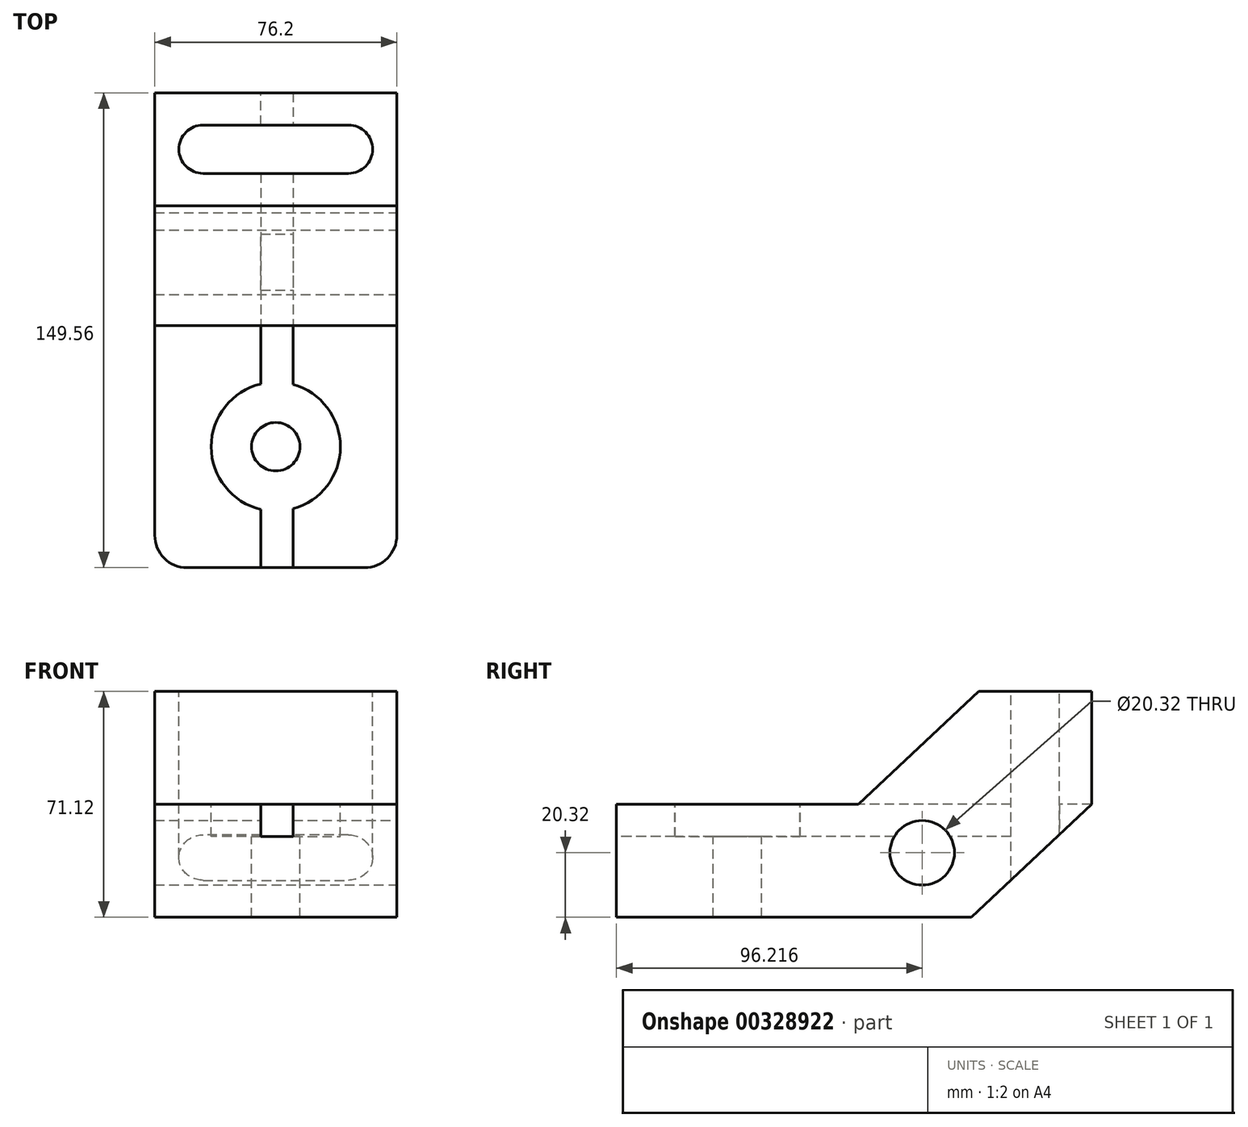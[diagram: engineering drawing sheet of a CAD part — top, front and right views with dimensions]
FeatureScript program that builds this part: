
annotation { "Feature Type Name" : "Feature", "Feature Type Description" : "" }
export const myFeature = defineFeature(function(context is Context, id is Id, definition is map)
    precondition{}
    {
        {
            var Q0;
            Q0=qCreatedBy(makeId("Right.planeOp"),FACE);
            var sketch = newSketch(context, id + "F0", { "sketchPlane" : qUnion([Q0])});
            skLineSegment(sketch, "E0.top", {"start": v(0, 35.56) * mm, "end": v(76.2, 35.56) * mm});
            skLineSegment(sketch, "E0.left", {"start": v(0, 0) * mm, "end": v(0, 35.56) * mm});
            skLineSegment(sketch, "E1", {"start": v(0, 0) * mm, "end": v(111.76, 0) * mm});
            skLineSegment(sketch, "E2", {"start": v(111.76, 0) * mm, "end": v(149.56, 35.56) * mm});
            skLineSegment(sketch, "E3", {"start": v(149.56, 35.56) * mm, "end": v(149.56, 71.12) * mm});
            skLineSegment(sketch, "E4", {"start": v(149.56, 71.12) * mm, "end": v(114, 71.12) * mm});
            skLineSegment(sketch, "E5", {"start": v(114, 71.12) * mm, "end": v(76.2, 35.56) * mm});
            skSolve(sketch);
        }
        {
            var Q0;
            Q0=makeQuery(id+"F0.imprint","IMPRINT",FACE,{"disambiguationData":[TD([[makeQuery(id+"F0.imprint","IMPRINT",EDGE,{"derivedFrom":sQuery(id+"F0.wireOp",EDGE,"E0.top")}),-1.0]])]});
            extrude(context, id + "F1", {"entities" : qUnion([Q0]), "oppositeDirection" : true, "depth" : 76.2 * mm});
        }
        {
            var Q0;
            Q0=makeQuery(id+"F1.opExtrude","CAP_EDGE",EDGE,{"disambiguationData":[OSD([sQuery(id+"F0.wireOp",EDGE,"E0.left")])],"isStart":false});
            var Q1;
            Q1=makeQuery(id+"F1.opExtrude","CAP_EDGE",EDGE,{"disambiguationData":[OSD([sQuery(id+"F0.wireOp",EDGE,"E0.left")])],"isStart":true});
            fillet(context, id + "F2", {"entities" : qUnion([Q0, Q1]), "radius" : 10.16 * mm, "tangentPropagation" : true, "allowEdgeOverflow" : false});
        }
        {
            var Q0;
            Q0=makeQuery(id+"F1.opExtrude","SWEPT_FACE",FACE,{"disambiguationData":[OSD([sQuery(id+"F0.wireOp",EDGE,"E0.top")])]});
            var sketch = newSketch(context, id + "F3", { "sketchPlane" : qUnion([Q0])});
            skCircle(sketch, "E6", {"center": v(-38.1, 38.1) * mm, "radius": 13.54 * mm});
            skLineSegment(sketch, "E7", {"start": v(-38.1, 38.1) * mm, "end": v(-33.02, 38.1) * mm});
            skLineSegment(sketch, "E8", {"start": v(-38.1, 38.1) * mm, "end": v(-43.18, 38.1) * mm});
            skLineSegment(sketch, "E9", {"start": v(-43.18, 38.1) * mm, "end": v(-43.18, 0) * mm});
            skLineSegment(sketch, "E10", {"start": v(-43.18, 0) * mm, "end": v(-33.02, 0) * mm});
            skLineSegment(sketch, "E11", {"start": v(-33.02, 0) * mm, "end": v(-33.02, 38.1) * mm});
            skLineSegment(sketch, "E12", {"start": v(-33.02, 38.1) * mm, "end": v(-33.02, 155.7) * mm});
            skLineSegment(sketch, "E13", {"start": v(-33.02, 155.7) * mm, "end": v(-43.18, 155.7) * mm});
            skLineSegment(sketch, "E14", {"start": v(-43.18, 155.7) * mm, "end": v(-43.18, 38.1) * mm});
            skSolve(sketch);
        }
        {
            var Q0;
            Q0=sQuery(id+"F3.wireOp",VERTEX,"E6.center");
            var Q1;
            Q1=makeQuery(id+"F1.opExtrude","SWEPT_BODY",BODY,{"disambiguationData":[OSD([sQuery(id+"F0.wireOp",EDGE,"E0.top"),sQuery(id+"F0.wireOp",EDGE,"E0.left"),sQuery(id+"F0.wireOp",EDGE,"E1"),sQuery(id+"F0.wireOp",EDGE,"E2"),sQuery(id+"F0.wireOp",EDGE,"E3"),sQuery(id+"F0.wireOp",EDGE,"E4"),sQuery(id+"F0.wireOp",EDGE,"E5")])]});
            hole(context, id + "F4", {"style" : HoleStyle.C_BORE, "endStyle" : HoleEndStyle.THROUGH, "holeDiameter" : 15.24 * mm, "cBoreDiameter" : 40.64 * mm, "cBoreDepth" : 10.16 * mm, "tappedDepth" : 12.7 * mm, "tapClearance" : 3, "locations" : qUnion([Q0]), "scope" : qUnion([Q1])});
        }
        {
            var Q0;
            Q0=makeQuery(id+"F1.opExtrude","CAP_FACE",FACE,{"disambiguationData":[OSD([sQuery(id+"F0.wireOp",EDGE,"E0.top"),sQuery(id+"F0.wireOp",EDGE,"E0.left"),sQuery(id+"F0.wireOp",EDGE,"E1"),sQuery(id+"F0.wireOp",EDGE,"E2"),sQuery(id+"F0.wireOp",EDGE,"E3"),sQuery(id+"F0.wireOp",EDGE,"E4"),sQuery(id+"F0.wireOp",EDGE,"E5")])],"isStart":true});
            var sketch = newSketch(context, id + "F5", { "sketchPlane" : qUnion([Q0])});
            skCircle(sketch, "E15", {"center": v(96.22, 20.32) * mm, "radius": 10.16 * mm});
            skSolve(sketch);
        }
        {
            var Q0;
            Q0=makeQuery(id+"F5.imprint","IMPRINT",FACE,{"disambiguationData":[TD([[makeQuery(id+"F5.imprint","IMPRINT",EDGE,{"derivedFrom":sQuery(id+"F5.wireOp",EDGE,"E15")}),1.0]])]});
            extrude(context, id + "F6", {"entities" : qUnion([Q0]), "operationType" : NewBodyOperationType.REMOVE, "endBound" : BoundingType.THROUGH_ALL, "oppositeDirection" : true, "depth" : 25.4 * mm});
        }
        {
            var Q0;
            Q0=makeQuery(id+"F1.opExtrude","SWEPT_FACE",FACE,{"disambiguationData":[OSD([sQuery(id+"F0.wireOp",EDGE,"E4")])]});
            var sketch = newSketch(context, id + "F7", { "sketchPlane" : qUnion([Q0])});
            skPoint(sketch, "E16.startSnap0", {"position": v(-38.1, 114) * mm});
            skArc(sketch, "E17", {"start": v(-60.96, 139.4) * mm, "mid": v(-68.58, 131.78) * mm, "end": v(-60.96, 124.16) * mm});
            skArc(sketch, "E18", {"start": v(-15.24, 124.16) * mm, "mid": v(-7.62, 131.78) * mm, "end": v(-15.24, 139.4) * mm});
            skLineSegment(sketch, "E19", {"start": v(-60.96, 139.4) * mm, "end": v(-15.24, 139.4) * mm});
            skLineSegment(sketch, "E20", {"start": v(-15.24, 124.16) * mm, "end": v(-60.96, 124.16) * mm});
            skSolve(sketch);
        }
        {
            var Q0;
            Q0=makeQuery(id+"F1.opExtrude","SWEPT_FACE",FACE,{"disambiguationData":[OSD([sQuery(id+"F0.wireOp",EDGE,"E0.left")])]});
            var sketch = newSketch(context, id + "F8", { "sketchPlane" : qUnion([Q0])});
            skLineSegment(sketch, "E21", {"start": v(-42.8, 35.56) * mm, "end": v(-42.8, 25.4) * mm});
            skLineSegment(sketch, "E22", {"start": v(-42.8, 25.4) * mm, "end": v(-32.64, 25.4) * mm});
            skLineSegment(sketch, "E23", {"start": v(-32.64, 25.4) * mm, "end": v(-32.64, 35.56) * mm});
            skLineSegment(sketch, "E24", {"start": v(-32.64, 35.56) * mm, "end": v(-42.8, 35.56) * mm});
            skSolve(sketch);
        }
        {
            var Q0;
            Q0=makeQuery(id+"F8.imprint","IMPRINT",FACE,{"disambiguationData":[TD([[makeQuery(id+"F8.imprint","IMPRINT",EDGE,{"derivedFrom":sQuery(id+"F8.wireOp",EDGE,"E21")}),1.0]])]});
            extrude(context, id + "F9", {"entities" : qUnion([Q0]), "operationType" : NewBodyOperationType.REMOVE, "endBound" : BoundingType.THROUGH_ALL, "oppositeDirection" : true, "depth" : 25.4 * mm});
        }
        {
            var Q0;
            Q0=makeQuery(id+"F7.imprint","IMPRINT",FACE,{"disambiguationData":[TD([[makeQuery(id+"F7.imprint","IMPRINT",EDGE,{"derivedFrom":sQuery(id+"F7.wireOp",EDGE,"E17")}),1.0]])]});
            extrude(context, id + "F10", {"entities" : qUnion([Q0]), "operationType" : NewBodyOperationType.REMOVE, "endBound" : BoundingType.THROUGH_ALL, "oppositeDirection" : true, "depth" : 25.4 * mm});
        }
    });
